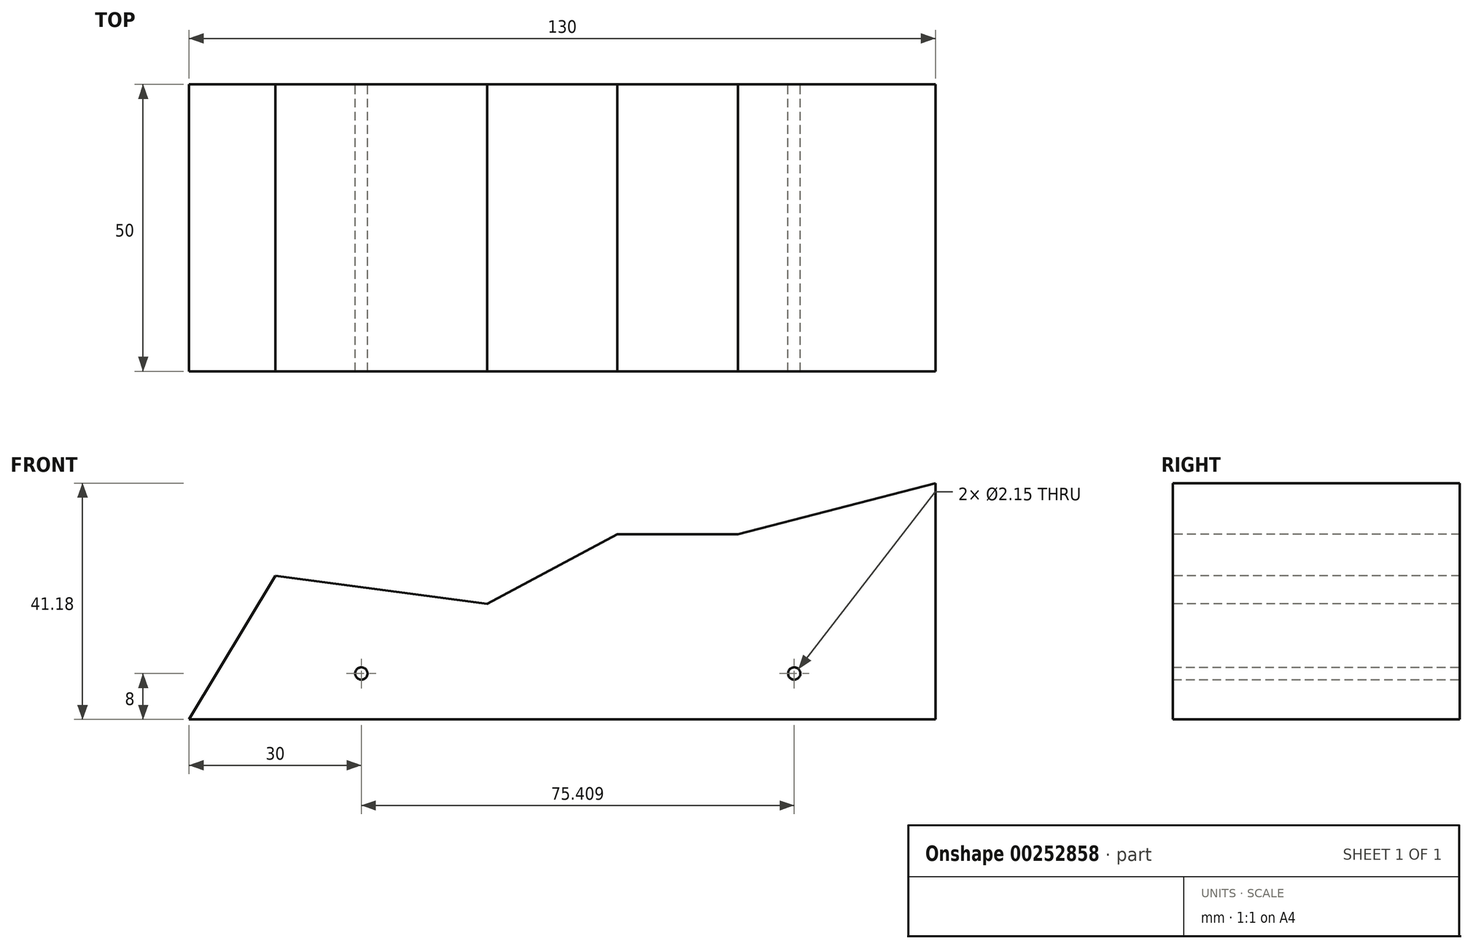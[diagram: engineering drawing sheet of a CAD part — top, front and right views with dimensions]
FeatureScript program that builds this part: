
annotation { "Feature Type Name" : "Feature", "Feature Type Description" : "" }
export const myFeature = defineFeature(function(context is Context, id is Id, definition is map)
    precondition{}
    {
        {
            var Q0;
            Q0=qCreatedBy(makeId("Front.planeOp"),FACE);
            var sketch = newSketch(context, id + "F0", { "sketchPlane" : qUnion([Q0])});
            skLineSegment(sketch, "E0.bottom", {"start": v(50, -25) * mm, "end": v(-50, -25) * mm});
            skLineSegment(sketch, "E0.top", {"start": v(50, 25) * mm, "end": v(-50, 25) * mm});
            skLineSegment(sketch, "E0.left", {"start": v(50, -25) * mm, "end": v(50, 25) * mm});
            skPoint(sketch, "E0.middle", {"position": v(0, 0) * mm});
            skLineSegment(sketch, "E1", {"start": v(-50, -25) * mm, "end": v(-80, -25) * mm});
            skLineSegment(sketch, "E2", {"start": v(-80, -25) * mm, "end": v(-50, 25) * mm});
            skLineSegment(sketch, "E3", {"start": v(50, -25) * mm, "end": v(25, -25) * mm});
            skCircle(sketch, "E4", {"center": v(-50, -17) * mm, "radius": 1.07 * mm});
            skCircle(sketch, "E5", {"center": v(25.4, -17) * mm, "radius": 1.08 * mm});
            skSolve(sketch);
        }
        {
            var Q0;
            Q0=makeQuery(id+"F0.imprint","IMPRINT",FACE,{"disambiguationData":[TD([[makeQuery(id+"F0.imprint","IMPRINT",EDGE,{"derivedFrom":sQuery(id+"F0.wireOp",EDGE,"E0.bottom")}),-1.0]])]});
            extrude(context, id + "F1", {"entities" : qUnion([Q0]), "depth" : 50 * mm});
        }
        {
            var Q0;
            Q0=makeQuery(id+"F1.opExtrude","CAP_FACE",FACE,{"disambiguationData":[OSD([sQuery(id+"F0.wireOp",EDGE,"E0.bottom"),sQuery(id+"F0.wireOp",EDGE,"E0.top"),sQuery(id+"F0.wireOp",EDGE,"E0.left"),sQuery(id+"F0.wireOp",EDGE,"E1"),sQuery(id+"F0.wireOp",EDGE,"E2"),sQuery(id+"F0.wireOp",EDGE,"E3"),sQuery(id+"F0.wireOp",EDGE,"E4"),sQuery(id+"F0.wireOp",EDGE,"E5")])],"isStart":false});
            var sketch = newSketch(context, id + "F2", { "sketchPlane" : qUnion([Q0])});
            skLineSegment(sketch, "E6", {"start": v(-65, 0) * mm, "end": v(-28.1, -4.83) * mm});
            skLineSegment(sketch, "E7", {"start": v(-28.1, -4.83) * mm, "end": v(-5.4, 7.24) * mm});
            skLineSegment(sketch, "E8", {"start": v(-5.4, 7.24) * mm, "end": v(15.61, 7.24) * mm});
            skLineSegment(sketch, "E9", {"start": v(15.61, 7.24) * mm, "end": v(50, 16.18) * mm});
            skSolve(sketch);
        }
        {
            var Q0;
            {var subQ1=sQuery(id+"F2.wireOp",EDGE,"E6");Q0=makeQuery(id+"F2.imprint","IMPRINT",FACE,{"disambiguationData":[TD([[makeQuery(id+"F2.imprint","IMPRINT",EDGE,{"derivedFrom":subQ1}),1.0]])]});}
            extrude(context, id + "F3", {"entities" : qUnion([Q0]), "operationType" : NewBodyOperationType.REMOVE, "oppositeDirection" : true, "depth" : 50 * mm});
        }
    });
